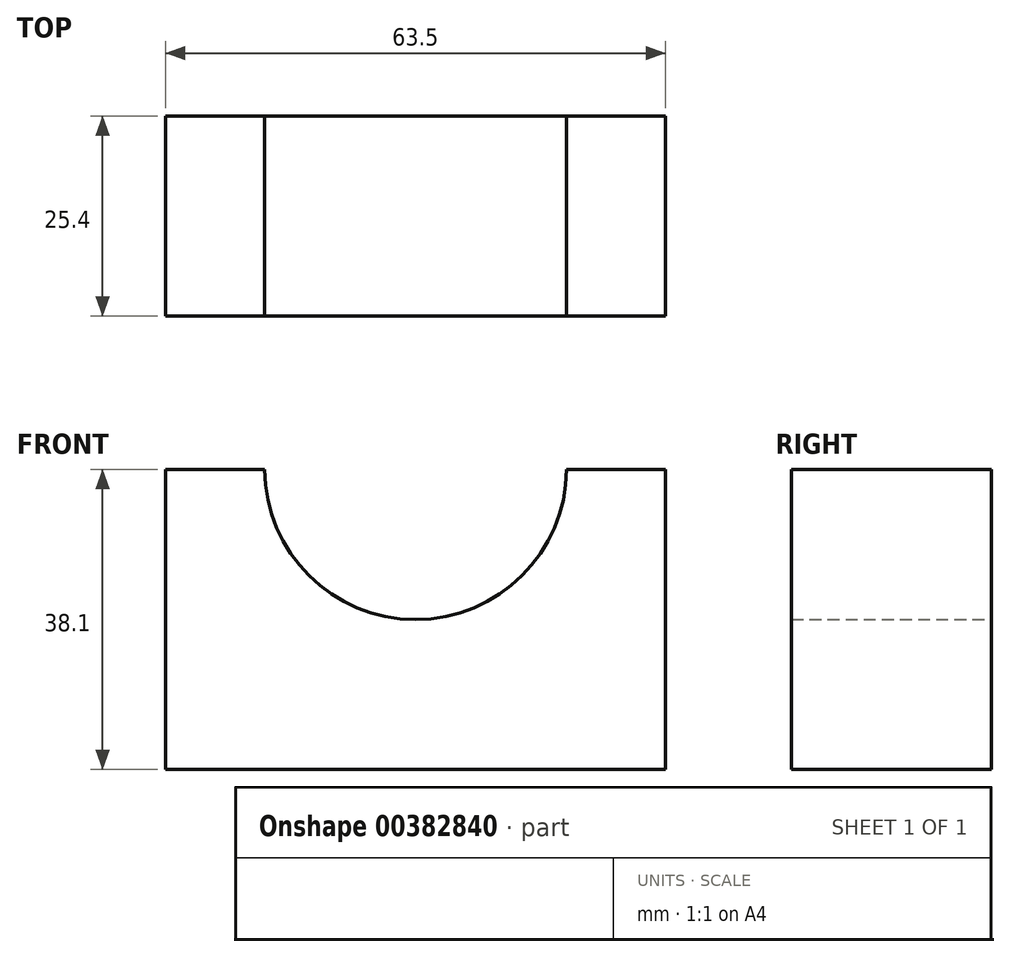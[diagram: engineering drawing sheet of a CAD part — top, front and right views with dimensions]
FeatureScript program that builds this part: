
annotation { "Feature Type Name" : "Feature", "Feature Type Description" : "" }
export const myFeature = defineFeature(function(context is Context, id is Id, definition is map)
    precondition{}
    {
        {
            var Q0;
            Q0=qCreatedBy(makeId("Front.planeOp"),FACE);
            var sketch = newSketch(context, id + "F0", { "sketchPlane" : qUnion([Q0])});
            skLineSegment(sketch, "E0", {"start": v(0, 0) * mm, "end": v(63.5, 0) * mm});
            skLineSegment(sketch, "E1", {"start": v(63.5, 0) * mm, "end": v(63.5, 38.1) * mm});
            skLineSegment(sketch, "E2", {"start": v(63.5, 38.1) * mm, "end": v(0, 38.1) * mm});
            skLineSegment(sketch, "E3", {"start": v(0, 38.1) * mm, "end": v(0, 0) * mm});
            skSolve(sketch);
        }
        {
            var Q0;
            Q0=qSketchRegion(id+"F0",true);
            extrude(context, id + "F1", {"entities" : qUnion([Q0]), "depth" : 25.4 * mm});
        }
        {
            var Q0;
            Q0=qCreatedBy(makeId("Front.planeOp"),FACE);
            var sketch = newSketch(context, id + "F2", { "sketchPlane" : qUnion([Q0])});
            skCircle(sketch, "E4", {"center": v(31.75, 38.23) * mm, "radius": 19.18 * mm});
            skSolve(sketch);
        }
        {
            var Q0;
            Q0=qSketchRegion(id+"F2",true);
            extrude(context, id + "F3", {"entities" : qUnion([Q0]), "operationType" : NewBodyOperationType.REMOVE, "depth" : 25.4 * mm});
        }
    });
